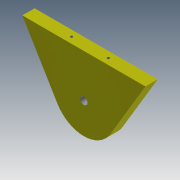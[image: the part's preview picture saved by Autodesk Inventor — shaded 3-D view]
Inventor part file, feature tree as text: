
AUTODESK INVENTOR PART (.ipt)
format: ipt  version: 2013 (Build 170138000, 138)  size: 90,624 bytes
history: native  units: mm
features: extrude x2, sketch x2
ambient origin geometry x8: Origin, YZ Plane, XZ Plane, XY Plane, X Axis, Y Axis, Z Axis, Center Point
bodies: Solid1 (feature_tree)
feature tree (4):
  extrude  "Extrusion1"  Depth=50.0mm
  extrude  "Extrusion2"  Depth=6.0mm
  sketch  "Sketch1"  dims[d4=50.0mm d5=50.0mm]
  sketch  "Sketch2"  dims[d6=100.0mm d7=6.0mm d8=10.0mm d9=0.0mm d11=2.0mm d12=2.0mm d13=10.0mm d14=0.0mm]
